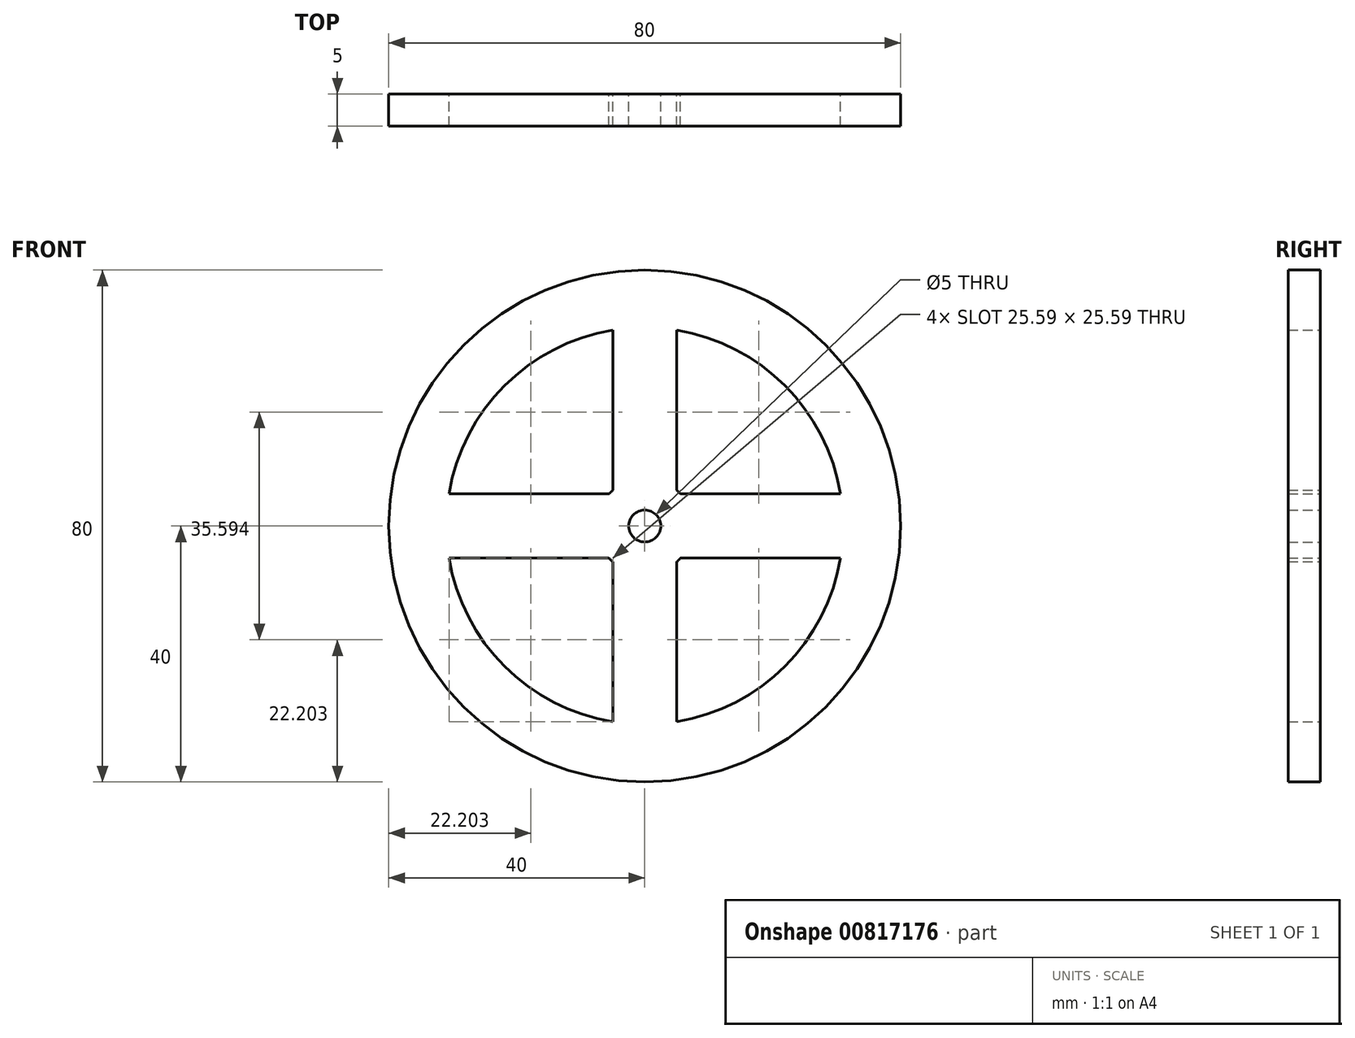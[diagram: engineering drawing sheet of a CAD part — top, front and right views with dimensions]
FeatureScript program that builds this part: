
annotation { "Feature Type Name" : "Feature", "Feature Type Description" : "" }
export const myFeature = defineFeature(function(context is Context, id is Id, definition is map)
    precondition{}
    {
        {
            var Q0;
            Q0=qCreatedBy(makeId("Front.planeOp"),FACE);
            var sketch = newSketch(context, id + "F0", { "sketchPlane" : qUnion([Q0])});
            skCircle(sketch, "E0", {"center": v(0, 0) * mm, "radius": 40 * mm});
            skArc(sketch, "E1", {"start": v(5, -5.6) * mm, "mid": v(5.3, -5.3) * mm, "end": v(5.6, -5) * mm});
            skArc(sketch, "E2", {"start": v(-30.6, -5) * mm, "mid": v(-21.92, -21.92) * mm, "end": v(-5, -30.6) * mm});
            skCircle(sketch, "E3", {"center": v(0, 0) * mm, "radius": 2.5 * mm});
            skLineSegment(sketch, "E4", {"start": v(0, 0) * mm, "end": v(0, 31) * mm, "construction": true});
            skLineSegment(sketch, "E5", {"start": v(0, 0) * mm, "end": v(31, 0) * mm, "construction": true});
            skLineSegment(sketch, "E6", {"start": v(0, 0) * mm, "end": v(0, -31) * mm, "construction": true});
            skLineSegment(sketch, "E7", {"start": v(0, 0) * mm, "end": v(-31, 0) * mm, "construction": true});
            skLineSegment(sketch, "E8.0", {"start": v(5, 5.6) * mm, "end": v(5, 30.6) * mm});
            skLineSegment(sketch, "E9.0", {"start": v(-5, 5.6) * mm, "end": v(-5, 30.6) * mm});
            skLineSegment(sketch, "E10.0", {"start": v(-5.6, 5) * mm, "end": v(-30.6, 5) * mm});
            skLineSegment(sketch, "E11.0", {"start": v(-5.6, -5) * mm, "end": v(-30.6, -5) * mm});
            skLineSegment(sketch, "E11.1", {"start": v(5.6, -5) * mm, "end": v(30.6, -5) * mm});
            skLineSegment(sketch, "E12.0", {"start": v(5, 5) * mm, "end": v(30.6, 5) * mm});
            skLineSegment(sketch, "E13.0", {"start": v(5, -5.6) * mm, "end": v(5, -30.6) * mm});
            skLineSegment(sketch, "E14.trimOffspring", {"start": v(5, 39.69) * mm, "end": v(5, 40) * mm});
            skLineSegment(sketch, "E15.trimOffspring", {"start": v(-5, 39.69) * mm, "end": v(-5, 40) * mm});
            skLineSegment(sketch, "E16.trimOffspring", {"start": v(-39.69, 5) * mm, "end": v(-40, 5) * mm});
            skLineSegment(sketch, "E17.trimOffspring", {"start": v(-39.69, -5) * mm, "end": v(-40, -5) * mm});
            skLineSegment(sketch, "E18.trimOffspring", {"start": v(-5, -39.69) * mm, "end": v(-5, -40) * mm});
            skLineSegment(sketch, "E19.trimOffspring", {"start": v(5, -39.69) * mm, "end": v(5, -40) * mm});
            skLineSegment(sketch, "E20.trimOffspring", {"start": v(39.69, -5) * mm, "end": v(40, -5) * mm});
            skLineSegment(sketch, "E21.trimOffspring", {"start": v(39.69, 5) * mm, "end": v(40, 5) * mm});
            skArc(sketch, "E22.trimOffspring", {"start": v(5, -30.6) * mm, "mid": v(21.92, -21.92) * mm, "end": v(30.6, -5) * mm});
            skArc(sketch, "E23.trimOffspring", {"start": v(30.6, 5) * mm, "mid": v(21.92, 21.92) * mm, "end": v(5, 30.6) * mm});
            skArc(sketch, "E24.trimOffspring", {"start": v(-5, 30.6) * mm, "mid": v(-21.92, 21.92) * mm, "end": v(-30.6, 5) * mm});
            skArc(sketch, "E25.trimOffspring", {"start": v(-5.6, -5) * mm, "mid": v(-5.3, -5.3) * mm, "end": v(-5, -5.6) * mm});
            skArc(sketch, "E26.trimOffspring", {"start": v(-5, 5.6) * mm, "mid": v(-5.3, 5.3) * mm, "end": v(-5.6, 5) * mm});
            skArc(sketch, "E27.trimOffspring", {"start": v(5.6, 5) * mm, "mid": v(5.3, 5.3) * mm, "end": v(5, 5.6) * mm});
            skLineSegment(sketch, "E28.trimOffspring", {"start": v(-5, -5.6) * mm, "end": v(-5, -30.6) * mm});
            skSolve(sketch);
        }
        {
            var Q0;
            Q0 = qSketchRegion(id + "F0", true);
            extrude(context, id + "F1", {"entities" : qUnion([Q0]), "endBound" : BoundingType.SYMMETRIC, "depth" : 5 * mm, "offsetDistance" : 25 * mm});
        }
    });
